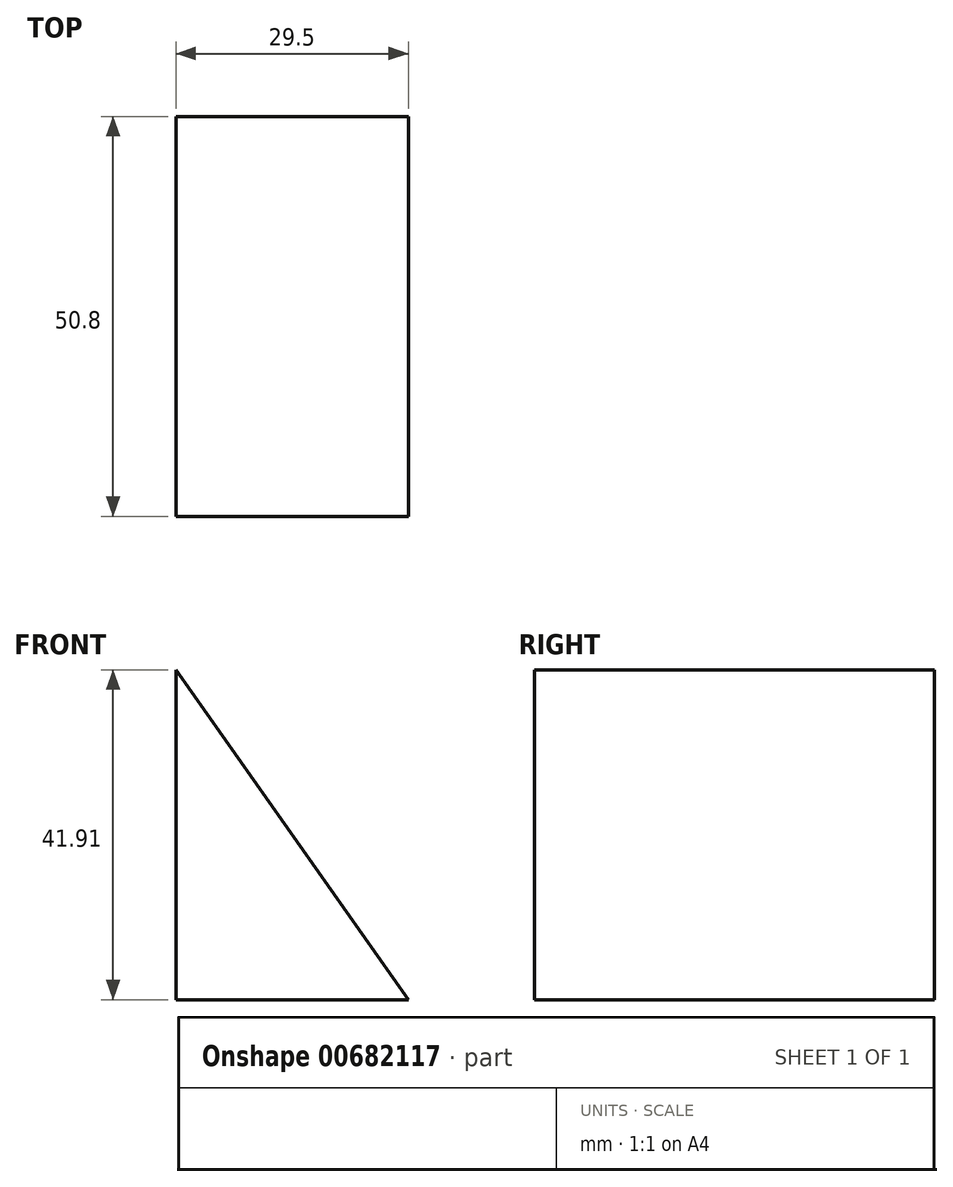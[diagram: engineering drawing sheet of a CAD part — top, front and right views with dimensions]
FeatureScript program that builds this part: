
annotation { "Feature Type Name" : "Feature", "Feature Type Description" : "" }
export const myFeature = defineFeature(function(context is Context, id is Id, definition is map)
    precondition{}
    {
        {
            var Q0;
            Q0=qCreatedBy(makeId("Front.planeOp"),FACE);
            var sketch = newSketch(context, id + "F0", { "sketchPlane" : qUnion([Q0])});
            skLineSegment(sketch, "E0", {"start": v(-29.5, 41.91) * mm, "end": v(-29.5, 0) * mm});
            skLineSegment(sketch, "E1", {"start": v(-29.5, 0) * mm, "end": v(0, 0) * mm});
            skLineSegment(sketch, "E2", {"start": v(0, 0) * mm, "end": v(-29.5, 41.91) * mm});
            skSolve(sketch);
        }
        {
            var Q0;
            Q0 = qSketchRegion(id + "F0", true);
            extrude(context, id + "F1", {"entities" : qUnion([Q0]), "depth" : 50.8 * mm, "offsetDistance" : 25.4 * mm});
        }
    });
